# Revit family: PRD_AR_ShwrFttngsPckg_F5EShowerPanel_F5ST2043
name_source: partatom
category: Plumbing Fixtures
units: mm (PartAtom-declared; Revit-internal decimal feet)

## family parameters
Cut with Voids When Loaded = No
Enable Cutting in Views = No
Host = Face
Maintain Annotation Orientation = No
OmniClass Number = 23.45.05.14.17.11
OmniClass Title = Shower Compartments
Part Type = Normal
Room Calculation Point = No
Round Connector Dimension = Use Diameter
Shared = No

## types (1)
- F5ST2043
    AccentColour = chrome-look (glossy)
    AdditionalConnections = No
    AdjustableFlowTime = Yes
    Adjustment = Yes
    AssetType = Fixed
    BIMObjectName = PRD_AR_ ShowerFittingsPackage_F5SShowerPanel_F5ST2043
    BasicColour = stainless steel-look
    BodyMaterial = PRD_AR_StainlessSteel_SatinFinished
    Category = Pr_40_20_87_75, Shower fittings package
    Circulation = No
    Color = stainless steel-look
    CompatibleA3000Open = No
    ConnectionWithPayWaterDispenser = not possible
    DN = 15  [stored 0.0492126 ft]
    Default Elevation = 1200 mm
    Description = F5S-Therm shower panel made of stainless steel for wall mounting with self-closing thermostatic mixer DN 15 and connecting nozzles for shower head. Especially suitable for facilities at risk of vandalism. Hydraulically controlled, for connection from the rear to hot and cold water. Function block with integrated FRAMIC self-closing cartridge, thermostat and mechanism for a water hygiene unit for automatic hygiene flushing, program-controlled thermal disinfection (additional bypass solenoid-operated flush valve cartridge necessary) and storage of statistical data. FRAMIC self-closing cartridge, low maintenance and stagnation free, with ceramic disc technology, self-closing, flow pressure independent due to medium-independent design. Stepless adjustment of flow duration. Thermostat with metal handle, an adjustable and turn-proof temperature stop and an option for manual thermal disinfection, visible parts polished chromium-plated. Connecting nozzles for the required additional DN 15 KWC shower head with pre-fitted flow regulator 9.0 l/min. Housing made of stainless steel, single-piece enclosed, including safety screws. Connecting hoses with lockable water volume control with backflow preventer and strainer.
    DiameterNominal = DN 15
    DrainSize = 15 mm  [stored 0.0492126 ft]
    Export Type to IFC As = IfcSanitaryTerminalType
    Features = For connection from the rear to hot and cold water. Visible parts polished chromium-plated. Housing dimensions 232 x 1160 x 90 mm. Shower head must be ordered separately.
    Finish = Satin finished
    FlowColdWater = 0.0 L/s
    FlowHotWater = 0.2 L/s
    ForHandShower = No
    FunctionalPrinciple = Hydraulic self-closing
    HasTray = No
    HygieneFlushing = prepared
    IfcExportAs = IfcSanitaryTerminalType
    IfcExportType = SHOWER
    InletSize = G 1/2 A
    LockingMechanism = Top section, ceramic
    Manufacturer = KWC Group Management AG
    ManufacturerName = KWC Group Management AG
    ManufacturerURL = www.kwc-professional.com
    Material = stainless steel
    MaterialCasing = stainless steel
    MaterialCodeCasing = 1.4301 Chrome Nickel steel V2A
    MaterialFitting = brass-look
    MaximumFlowTime = 35 Seconds
    MinimumFlowPressure = 1 bar
    MinimumFlowTime = 5 Seconds
    Model = F5ST2043
    ModelNumber = 2030068003
    ModelReference = F5ST2043
    NBSDescription = Shower fittings package
    NBSReference = 45-35-70/330
    Name = F5S Shower panel F5ST2043
    NominalDepth = 90 mm  [stored 0.295276 ft]
    NominalHeight = 1160 mm  [stored 3.80577 ft]
    NominalLength = 1160 mm  [stored 3.80577 ft]
    NominalWidth = 232 mm  [stored 0.761155 ft]
    OverallDepth = 90 mm
    OverallHeight = 1160 mm
    OverallWidth = 232 mm
    Parameterization = manual
    PositionOfWaterConnection = from backside
    ProductInformation = http://pim.kwc.com
    ProtectiveShutdown = No
    Push-button = No
    ShowerHead = for separately shower head
    ShowerPipeDraining = No
    ShowerType = Individual
    Size = 15
    SoundInsulation = No
    Status = NEW
    SurfaceFinishCasing = satin finished
    SurfaceFinishFitting = chromed
    SurfaceTreatmentFitting = polished
    TemperatureLimit = Yes
    ThermalDisinfection = manual
    Type IFC Predefined Type = SHOWER
    TypeOfMixing = with thermostat
    TypeOfMounting = wall mounting
    TypeOfOperation = manual operation
    TypeOfShower = shower panel
    URL = www.kwc-professional.com
    Uniclass2015Code = Pr_40_20_87_75
    Uniclass2015Title = Shower fittings package
    Uniclass2015Version = Products v1.36
    Version = 1
    VolumeFlowRateAt3Bar = 0.15 l/s
    WaterConnection = hose (gland nut)
    WithBackflowPreventer = Yes
    WithFilter = Yes
    WithRosettesCoverPlate = Yes
    WithShowerSet = No
    WithSoapDish = No

note: [stored X ft] marks values corroborated as IEEE doubles in the binary element streams (Revit-internal decimal feet)

## geometry (parser evidence)
native form markers: Sweep x5
no freeform markers — native parametric forms only
